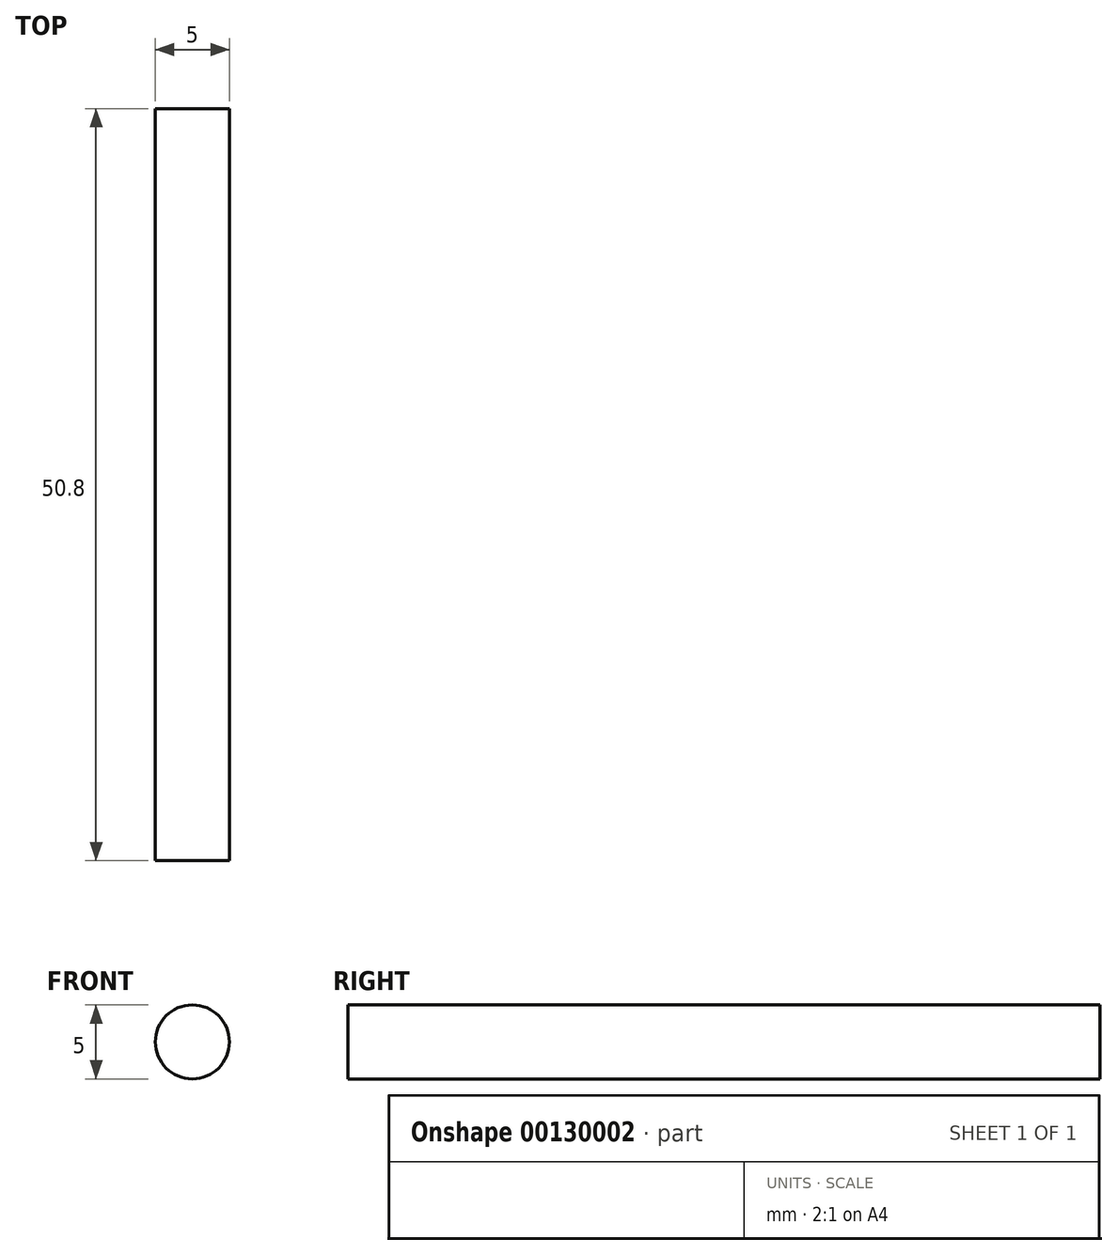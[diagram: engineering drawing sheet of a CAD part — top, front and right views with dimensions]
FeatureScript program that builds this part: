
annotation { "Feature Type Name" : "Feature", "Feature Type Description" : "" }
export const myFeature = defineFeature(function(context is Context, id is Id, definition is map)
    precondition{}
    {
        {
            var Q0;
            Q0=qCreatedBy(makeId("Front.planeOp"),FACE);
            var sketch = newSketch(context, id + "F0", { "sketchPlane" : qUnion([Q0])});
            skCircle(sketch, "E0", {"center": v(0, 0) * mm, "radius": 2.5 * mm});
            skSolve(sketch);
        }
        {
            var Q0;
            Q0 = qSketchRegion(id + "F0", true);
            extrude(context, id + "F1", {"entities" : qUnion([Q0]), "depth" : 50.8 * mm});
        }
    });
